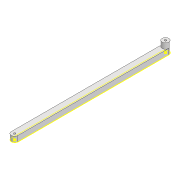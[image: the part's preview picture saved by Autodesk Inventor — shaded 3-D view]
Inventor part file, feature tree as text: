
AUTODESK INVENTOR PART (.ipt)
format: ipt  version: 2022 (Build 260153000, 153)  size: 105,472 bytes
history: native  units: mm
features: sketch x3, extrude x2, projected_geometry x2
ambient origin geometry x8: Origin, YZ Plane, XZ Plane, XY Plane, X Axis, Y Axis, Z Axis, Center Point
bodies: Solid1 (feature_tree)
feature tree (7):
  extrude  "Extrusion1"  Depth=10.0mm
  extrude  "Extrusion2"  Depth=3.0mm
  sketch  "Sketch3"  dims[d4=8.0mm d5=0.0mm d12=10.0mm d13=8.0mm d14=0.0mm]
  sketch  "Sketch1"  dims[d0=225.149mm d1=10.0mm]
  sketch  "Sketch2"  dims[d2=3.0mm d3=3.0mm]
  projected_geometry  "Projected Loop1"
  projected_geometry  "Projected Loop2"
